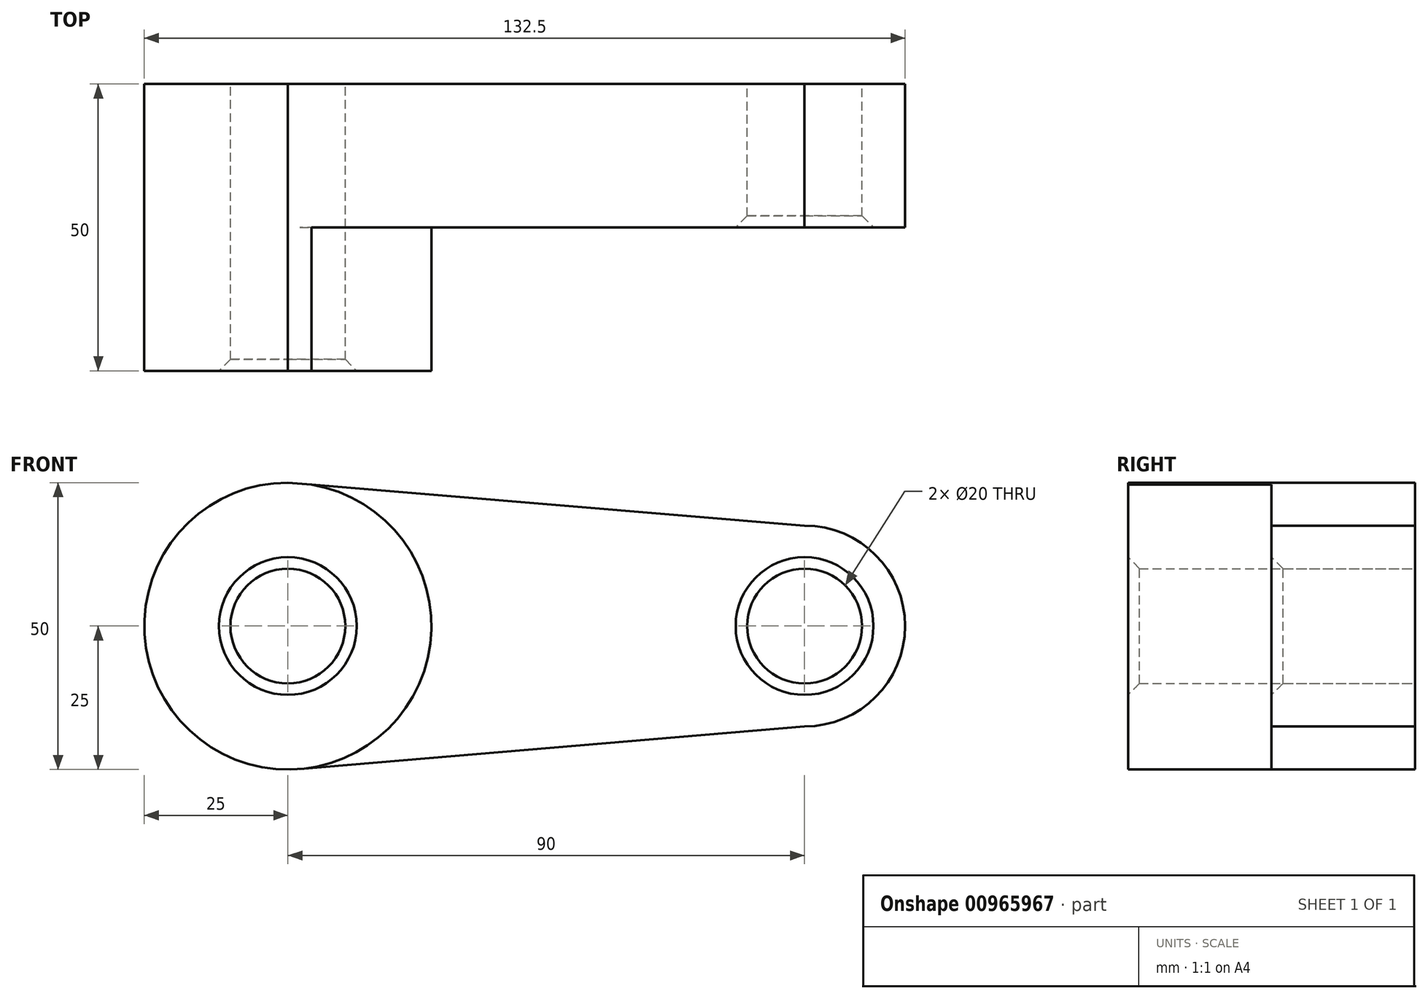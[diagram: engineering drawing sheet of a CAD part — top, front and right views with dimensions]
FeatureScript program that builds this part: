
annotation { "Feature Type Name" : "Feature", "Feature Type Description" : "" }
export const myFeature = defineFeature(function(context is Context, id is Id, definition is map)
    precondition{}
    {
        {
            var Q0;
            Q0=qCreatedBy(makeId("Front.planeOp"),FACE);
            var sketch = newSketch(context, id + "F0", { "sketchPlane" : qUnion([Q0])});
            skCircle(sketch, "E0", {"center": v(0, 0) * mm, "radius": 25 * mm});
            skCircle(sketch, "E1", {"center": v(90, 0) * mm, "radius": 17.5 * mm});
            skCircle(sketch, "E2", {"center": v(0, 0) * mm, "radius": 10 * mm});
            skCircle(sketch, "E3", {"center": v(90, 0) * mm, "radius": 10 * mm});
            skLineSegment(sketch, "E4", {"start": v(0, 25) * mm, "end": v(90, 17.5) * mm});
            skLineSegment(sketch, "E5", {"start": v(90, -17.5) * mm, "end": v(0, -25.09) * mm});
            skSolve(sketch);
        }
        {
            var Q0;
            Q0=makeQuery(id+"F0.imprint","IMPRINT",FACE,{"disambiguationData":[TD([[makeQuery(id+"F0.imprint","IMPRINT",EDGE,{"derivedFrom":sQuery(id+"F0.wireOp",EDGE,"E2")}),-1.0]])]});
            var Q1;
            {var subQ0=sQuery(id+"F0.wireOp",EDGE,"E5");var subQ1=sQuery(id+"F0.wireOp",EDGE,"E0");var subQ2=makeQuery(id+"F0.imprint","INTERSECT",VERTEX,{"derivedFrom":[subQ1,subQ0]});Q1=makeQuery(id+"F0.imprint","IMPRINT",FACE,{"disambiguationData":[TD([[makeQuery(id+"F0.imprint","IMPRINT",EDGE,{"disambiguationData":[TD([[subQ2,-1.0]])],"derivedFrom":subQ1}),-1.0]])]});}
            var Q2;
            Q2=makeQuery(id+"F0.imprint","IMPRINT",FACE,{"disambiguationData":[TD([[makeQuery(id+"F0.imprint","IMPRINT",EDGE,{"derivedFrom":sQuery(id+"F0.wireOp",EDGE,"E3")}),-1.0]])]});
            extrude(context, id + "F1", {"entities" : qUnion([Q0, Q1, Q2]), "depth" : 25 * mm, "offsetDistance" : 25 * mm});
        }
        {
            var Q0;
            Q0=makeQuery(id+"F0.imprint","IMPRINT",FACE,{"disambiguationData":[TD([[makeQuery(id+"F0.imprint","IMPRINT",EDGE,{"derivedFrom":sQuery(id+"F0.wireOp",EDGE,"E2")}),-1.0]])]});
            extrude(context, id + "F2", {"entities" : qUnion([Q0]), "operationType" : NewBodyOperationType.ADD, "depth" : 50 * mm, "offsetDistance" : 25 * mm});
        }
        {
            var Q0;
            Q0=makeQuery(id+"F2.opExtrude","CAP_EDGE",EDGE,{"disambiguationData":[OSD([sQuery(id+"F0.wireOp",EDGE,"E2")])],"isStart":false});
            var Q1;
            Q1=makeQuery(id+"F1.opExtrude","CAP_EDGE",EDGE,{"disambiguationData":[OSD([sQuery(id+"F0.wireOp",EDGE,"E3")])],"isStart":false});
            chamfer(context, id + "F3", {"entities" : qUnion([Q0, Q1]), "width" : 2 * mm, "tangentPropagation" : true});
        }
    });
